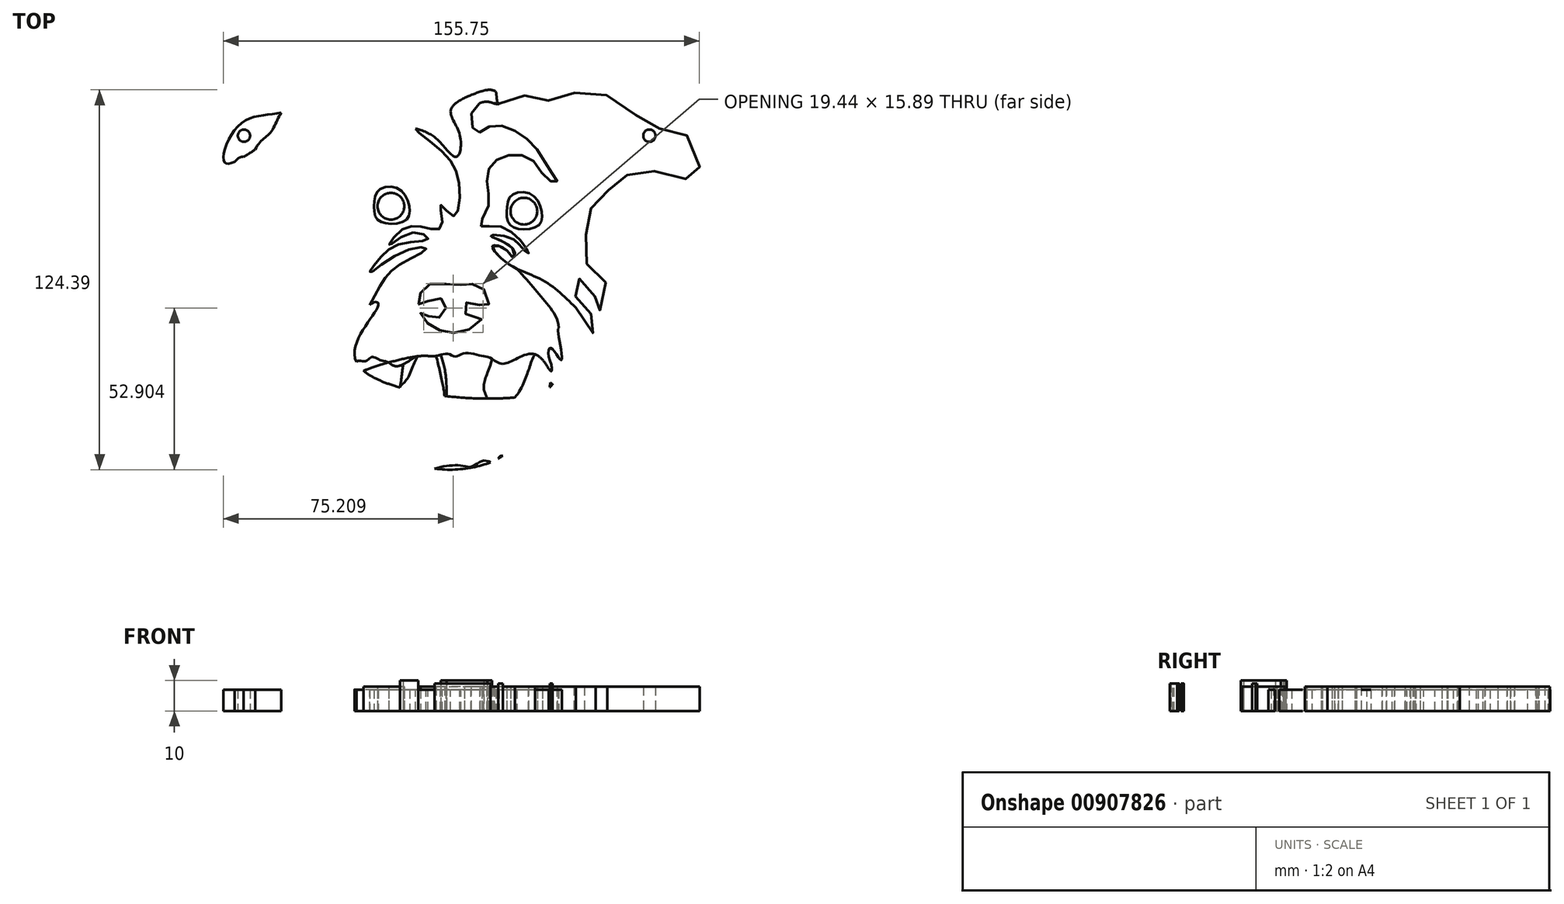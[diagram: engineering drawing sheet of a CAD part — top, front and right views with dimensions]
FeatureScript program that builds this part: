
annotation { "Feature Type Name" : "Feature", "Feature Type Description" : "" }
export const myFeature = defineFeature(function(context is Context, id is Id, definition is map)
    precondition{}
    {
        {
            var Q0;
            Q0=qCreatedBy(makeId("Top.planeOp"),FACE);
            var sketch = newSketch(context, id + "F0", { "sketchPlane" : qUnion([Q0])});
            skFitSpline(sketch, "E0", {"points": [v(-10.8, -4.8) * mm, v(-6.27, 3.26) * mm, v(0, 8.97) * mm, v(7.61, 13.52) * mm, v(0, 12.57) * mm, v(-10.8, 5.73) * mm, v(-8.15, 9.81) * mm, v(0, 15.35) * mm, v(8.27, 16.8) * mm, v(2.9, 18.78) * mm, v(-4.45, 14.71) * mm, v(0, 19.94) * mm, v(7.46, 20.4) * mm, v(12.68, 20.87) * mm, v(12.37, 27.92) * mm, v(16.54, 24.23) * mm, v(18.41, 34.41) * mm, v(12.68, 45.55) * mm, v(4.16, 52.76) * mm, v(7.78, 51.65) * mm, v(12.74, 47.87) * mm, v(17.51, 43.68) * mm, v(18.68, 50.57) * mm, v(15.7, 58.97) * mm, v(23.33, 64.27) * mm, v(30.48, 64.9) * mm, v(31.5, 61.05) * mm, v(27.68, 61.69) * mm, v(22.54, 58.18) * mm, v(24.15, 51.63) * mm, v(28.4, 53.58) * mm, v(36.06, 52.49) * mm, v(43.55, 46.57) * mm, v(48.61, 38.67) * mm, v(50.45, 35.49) * mm, v(47.6, 36.07) * mm, v(42.15, 42.8) * mm, v(34.73, 44.14) * mm, v(28.78, 40.89) * mm, v(27.59, 34.03) * mm, v(27.86, 27.2) * mm, v(25.33, 21.09) * mm, v(31.5, 20.96) * mm, v(39.88, 14.46) * mm, v(41.11, 12.07) * mm, v(38.85, 13.96) * mm, v(35.11, 17.25) * mm, v(28.71, 17.86) * mm, v(36.07, 13.55) * mm, v(36.16, 10.73) * mm, v(33.75, 13.27) * mm, v(29.39, 14.45) * mm, v(31.5, 11.05) * mm, v(37.36, 6.94) * mm, v(44.52, 3.89) * mm, v(50.99, -0.43) * mm, v(56.57, -5.75) * mm], "startDerivative": vector(204.5, 377.81) * mm, "endDerivative": vector(287.63, -276.69) * mm});
            skFitSpline(sketch, "E1", {"points": [v(8.8, 1.95) * mm, v(5.37, -1.97) * mm, v(5.52, -4.91) * mm, v(10.58, -2.48) * mm, v(14, -4.45) * mm, v(12.53, -8.54) * mm, v(9.6, -9.02) * mm, v(5.84, -7.37) * mm, v(7.8, -10.65) * mm, v(13.5, -13.46) * mm, v(20.67, -13.32) * mm, v(25.9, -9.08) * mm, v(23.61, -8.9) * mm, v(20.36, -7.42) * mm, v(21.5, -3.66) * mm, v(27.53, -5.65) * mm, v(26.73, 0) * mm, v(21.85, 2.07) * mm, v(17.44, 1.76) * mm, v(8.8, 1.95) * mm]});
            skFitSpline(sketch, "E2", {"points": [v(1.18, 23.1) * mm, v(2.05, 27.69) * mm, v(-1.63, 33.35) * mm, v(-7.8, 32.82) * mm, v(-9.32, 28.56) * mm, v(-8.65, 23.6) * mm, v(-4.68, 21.8) * mm, v(1.18, 23.1) * mm]});
            skFitSpline(sketch, "E3", {"points": [v(44.57, 21.3) * mm, v(45.44, 25.89) * mm, v(41.75, 31.54) * mm, v(35.58, 31.01) * mm, v(34.06, 26.75) * mm, v(34.73, 21.8) * mm, v(38.7, 19.99) * mm, v(44.57, 21.3) * mm]});
            skFitSpline(sketch, "E4", {"points": [v(-39.8, 58.13) * mm, v(-43.2, 51.74) * mm, v(-47.26, 47.79) * mm, v(-50.4, 42.92) * mm, v(-52.33, 43.63) * mm, v(-56.15, 40.35) * mm], "startDerivative": vector(-14.9, -24.98) * mm, "endDerivative": vector(-17.36, -29.51) * mm});
            skCircle(sketch, "E5", {"center": v(-3.88, 27.48) * mm, "radius": 4.38 * mm});
            skCircle(sketch, "E6", {"center": v(39.61, 25.85) * mm, "radius": 4.38 * mm});
            skFitSpline(sketch, "E7.trimOffspring", {"points": [v(-53.58, 42.72) * mm, v(-38.46, 50.37) * mm, v(-36.8, 41.61) * mm, v(-29.18, 37.15) * mm, v(-26.98, 27.78) * mm, v(-25.92, 22.85) * mm, v(-32.23, 11.83) * mm, v(-35, 4.15) * mm, v(-39.11, -7.41) * mm, v(-35.05, -17) * mm, v(-33.9, -6.88) * mm, v(-30.1, -3.66) * mm, v(-29.82, -7.15) * mm, v(-31.18, -15.42) * mm, v(-26.03, -25.03) * mm, v(-28.42, -13.22) * mm, v(-25.45, -8.9) * mm, v(-24.9, -17.09) * mm, v(-21.64, -29.95) * mm, v(-21.75, -14.74) * mm, v(-18.15, -10.31) * mm, v(-16.36, -15.67) * mm, v(-10.8, -4.8) * mm, v(-7.98, -4.63) * mm, v(-15.2, -23.55) * mm, v(47.9, -31.99) * mm, v(47.73, -21.57) * mm, v(48.51, -18.94) * mm, v(51.72, -22.93) * mm, v(51.36, -17.05) * mm, v(51.05, -12.37) * mm, v(54.1, -14.13) * mm, v(59.32, -20.41) * mm, v(57.39, -12) * mm, v(56.56, -5.73) * mm, v(62.83, -14.58) * mm, v(59.75, -4.42) * mm, v(56.29, -1.7) * mm, v(57.41, 3.6) * mm, v(62.47, -0.53) * mm, v(63.7, -7.26) * mm, v(66.76, 1.24) * mm, v(60.44, 8.2) * mm, v(60.2, 19.77) * mm, v(62.4, 28.3) * mm, v(69.28, 34.33) * mm, v(75.06, 38.45) * mm, v(88.21, 37.84) * mm, v(96.19, 36.7) * mm, v(94.02, 49.67) * mm, v(83.59, 53) * mm, v(74.28, 58.82) * mm, v(59.76, 65.5) * mm, v(48.51, 61.93) * mm, v(41.1, 63.9) * mm, v(31.5, 61.05) * mm, v(30.5, 64.89) * mm, v(27.96, 67.2) * mm, v(17.53, 66.47) * mm, v(12.86, 62.32) * mm, v(4.92, 67.63) * mm, v(2.17, 64.3) * mm, v(-4.68, 62.96) * mm, v(-8.27, 61.58) * mm, v(-18.94, 67.15) * mm, v(-29.1, 63.32) * mm, v(-39.8, 58.13) * mm, v(-53.18, 54.38) * mm, v(-58.52, 42.2) * mm, v(-53.58, 42.72) * mm]});
            skCircle(sketch, "E8", {"center": v(-51.96, 50.57) * mm, "radius": 2 * mm});
            skLineSegment(sketch, "E9", {"start": v(-51.96, 50.57) * mm, "end": v(80.66, 50.57) * mm, "construction": true});
            skCircle(sketch, "E10", {"center": v(80.66, 50.57) * mm, "radius": 2 * mm});
            skPoint(sketch, "E11.startDerivative.orphan", {"position": v(46.68, -34.89) * mm});
            skPoint(sketch, "E12.23.internal.orphan", {"position": v(-8.15, -6.56) * mm});
            skPoint(sketch, "E12.45.internal.orphan", {"position": v(66.75, 0) * mm});
            skPoint(sketch, "E12.5.internal.orphan", {"position": v(-25.9, 21.6) * mm});
            skFitSpline(sketch, "E13", {"points": [v(48.07, -31.84) * mm, v(47.73, -25.71) * mm, v(43.27, -21.01) * mm, v(36.6, -22.74) * mm, v(31.89, -24.02) * mm, v(28.43, -22.1) * mm, v(25.22, -21.45) * mm, v(20.4, -20.58) * mm, v(17.3, -21.71) * mm, v(14.66, -20.83) * mm, v(10.88, -21.54) * mm, v(5.07, -21.63) * mm, v(-13.12, -26.56) * mm], "startDerivative": vector(16.73, 149.66) * mm, "endDerivative": vector(-59.85, -28.24) * mm});
            skFitSpline(sketch, "E14", {"points": [v(-11.13, -25.98) * mm, v(-2.47, -37.25) * mm, v(-2.3, -42.9) * mm, v(-0.8, -48.97) * mm, v(2.37, -53.28) * mm, v(7.48, -55.7) * mm, v(10.82, -55.22) * mm, v(16.1, -55.92) * mm, v(18.48, -55.4) * mm, v(21.3, -54.25) * mm, v(24.73, -50.64) * mm, v(27.54, -46.24) * mm, v(27.28, -42.02) * mm, v(28.34, -37.97) * mm, v(26.49, -31.8) * mm, v(29.15, -22.5) * mm], "startDerivative": vector(45.21, -72.34) * mm, "endDerivative": vector(22.44, 125.56) * mm});
            skFitSpline(sketch, "E15", {"points": [v(-2.47, -37.25) * mm, v(-0.97, -31.84) * mm, v(0.45, -23.07) * mm], "startDerivative": vector(-0.31, 9) * mm, "endDerivative": vector(3.22, 7.67) * mm});
            skFitSpline(sketch, "E16", {"points": [v(10.88, -21.54) * mm, v(13.16, -31.45) * mm, v(13.6, -37.25) * mm, v(12.04, -48.13) * mm, v(12.29, -50) * mm, v(13.42, -45.91) * mm, v(14.28, -31.84) * mm, v(13.48, -24.82) * mm, v(12.42, -21.16) * mm], "startDerivative": vector(18.26, -65.77) * mm, "endDerivative": vector(-11.6, 37.87) * mm});
            skFitSpline(sketch, "E17", {"points": [v(-21.75, -14.74) * mm, v(-18.15, -32.84) * mm, v(-10.83, -43.87) * mm, v(-8.52, -51.1) * mm, v(-6.1, -54.56) * mm, v(-4.05, -53.13) * mm, v(-1.19, -58.8) * mm, v(2.45, -56.73) * mm, v(6.48, -58.59) * mm, v(12.34, -57.95) * mm, v(19.06, -57.47) * mm, v(22.65, -57.77) * mm, v(26.74, -55.8) * mm, v(30.13, -56.63) * mm, v(31.89, -54.36) * mm, v(34.45, -54.33) * mm, v(39.8, -47.91) * mm, v(45.11, -40.35) * mm, v(47.73, -25.71) * mm], "startDerivative": vector(14.83, -144.66) * mm, "endDerivative": vector(20.53, 124.04) * mm});
            skFitSpline(sketch, "E18", {"points": [v(-21.64, -29.95) * mm, v(-21.77, -32.8) * mm, v(-21.65, -40.38) * mm, v(-8.75, -50.33) * mm, v(9.3, -58.25) * mm, v(28.4, -56.49) * mm, v(39.8, -47.91) * mm, v(48.07, -31.84) * mm], "startDerivative": vector(-2.7, -16.77) * mm, "endDerivative": vector(-32.2, 87.54) * mm});
            skFitSpline(sketch, "E19", {"points": [v(-21.7, -31.76) * mm, v(-20.96, -30.57) * mm, v(-19.47, -29.17) * mm], "startDerivative": vector(1.6, 2.32) * mm, "endDerivative": vector(0.83, 1.94) * mm});
            skFitSpline(sketch, "E20", {"points": [v(7.48, -55.7) * mm, v(0.94, -54.98) * mm, v(-3.23, -52.53) * mm, v(-4.81, -46.85) * mm, v(-6.3, -43.16) * mm, v(-8.77, -37.79) * mm, v(-10.27, -31.89) * mm, v(-12.43, -26.75) * mm], "startDerivative": vector(-37.93, 0.45) * mm, "endDerivative": vector(-25.79, 34.44) * mm});
            skFitSpline(sketch, "E21", {"points": [v(5.07, -21.63) * mm, v(1.63, -28.75) * mm, v(-0.97, -31.84) * mm], "startDerivative": vector(-5.85, -5.23) * mm, "endDerivative": vector(-4.71, -8.1) * mm});
            skFitSpline(sketch, "E22", {"points": [v(5.07, -21.63) * mm, v(1.09, -23.8) * mm, v(-2.67, -24.86) * mm, v(-4.94, -23.53) * mm, v(-7.66, -22.8) * mm, v(-10.22, -21.88) * mm, v(-12.36, -23.26) * mm, v(-15.2, -23.55) * mm], "startDerivative": vector(-20.84, -2.18) * mm, "endDerivative": vector(-14.68, -20.72) * mm});
            skFitSpline(sketch, "E23", {"points": [v(48.57, -24.37) * mm, v(48.6, -26.55) * mm, v(47.73, -25.71) * mm], "startDerivative": vector(0.43, -1.1) * mm, "endDerivative": vector(-0.72, 0.67) * mm});
            skLineSegment(sketch, "E24.trimOffspring", {"start": v(51.23, -22.45) * mm, "end": v(51.23, -22.45) * mm});
            skFitSpline(sketch, "E25.trimOffspring", {"points": [v(30.15, 61.06) * mm, v(29.84, 61.06) * mm, v(31.5, 61.05) * mm], "startDerivative": vector(2.35, 0.22) * mm, "endDerivative": vector(2.29, -1.15) * mm});
            skFitSpline(sketch, "E26.trimOffspring", {"points": [v(-10.8, -4.8) * mm, v(-6.27, 3.26) * mm, v(0, 8.97) * mm, v(7.61, 13.52) * mm, v(0, 12.57) * mm, v(-10.8, 5.73) * mm, v(-8.15, 9.81) * mm, v(0, 15.35) * mm, v(8.27, 16.8) * mm, v(2.9, 18.78) * mm, v(-4.45, 14.71) * mm, v(0, 19.94) * mm, v(7.46, 20.4) * mm, v(12.68, 20.87) * mm, v(12.37, 27.92) * mm, v(16.54, 24.23) * mm, v(18.41, 34.41) * mm, v(12.68, 45.55) * mm, v(4.16, 52.76) * mm, v(7.78, 51.65) * mm, v(12.74, 47.87) * mm, v(17.51, 43.68) * mm, v(18.68, 50.62) * mm, v(15.7, 58.97) * mm, v(23.33, 64.27) * mm, v(30.48, 64.9) * mm, v(31.5, 61.05) * mm, v(27.68, 61.69) * mm, v(22.54, 58.18) * mm, v(24.15, 51.63) * mm, v(28.4, 53.58) * mm, v(36.06, 52.49) * mm, v(43.55, 46.57) * mm, v(48.61, 38.67) * mm, v(50.45, 35.49) * mm, v(47.6, 36.07) * mm, v(42.15, 42.8) * mm, v(34.73, 44.14) * mm, v(28.78, 40.89) * mm, v(27.59, 34.03) * mm, v(27.86, 27.2) * mm, v(25.33, 21.09) * mm, v(31.5, 20.96) * mm, v(39.88, 14.46) * mm, v(41.11, 12.07) * mm, v(38.85, 13.96) * mm, v(35.11, 17.25) * mm, v(28.71, 17.86) * mm, v(36.07, 13.55) * mm, v(36.16, 10.73) * mm, v(33.75, 13.27) * mm, v(29.39, 14.45) * mm, v(31.5, 11.05) * mm, v(37.36, 6.94) * mm, v(44.52, 3.89) * mm, v(50.99, -0.43) * mm, v(56.57, -5.75) * mm], "startDerivative": vector(204.5, 377.81) * mm, "endDerivative": vector(287.63, -276.69) * mm});
            skLineSegment(sketch, "E27", {"start": v(-8.75, -50.33) * mm, "end": v(38.15, -50.33) * mm, "construction": true});
            skFitSpline(sketch, "E28", {"points": [v(38.15, -50.33) * mm, v(48.61, -43.38) * mm, v(50.14, -40.66) * mm, v(50.77, -38.4) * mm, v(50.88, -34.2) * mm, v(50.82, -32.87) * mm, v(49.65, -31.36) * mm, v(47.21, -29.67) * mm], "startDerivative": vector(50.7, 11.43) * mm, "endDerivative": vector(-15.7, 6.64) * mm});
            skFitSpline(sketch, "E29", {"points": [v(0.94, -54.98) * mm, v(7.36, -56.11) * mm, v(10.41, -55.7) * mm], "startDerivative": vector(11.84, -2.87) * mm, "endDerivative": vector(6.81, 1.99) * mm});
            skFitSpline(sketch, "E30.trimOffspring", {"points": [v(7.48, -55.57) * mm, v(10.4, -55.69) * mm, v(12.88, -56.53) * mm, v(18.22, -56.58) * mm, v(25.86, -54.07) * mm, v(28.17, -51.56) * mm, v(30, -45.33) * mm, v(32.67, -39.36) * mm, v(37.27, -34.44) * mm, v(40.1, -29) * mm, v(41.56, -24.92) * mm, v(43.27, -21.01) * mm], "startDerivative": vector(44.21, 4.46) * mm, "endDerivative": vector(27.63, 35.75) * mm});
            skFitSpline(sketch, "E31", {"points": [v(37.36, 6.94) * mm, v(43.45, 0) * mm, v(48.1, -5.63) * mm, v(51.05, -12.37) * mm], "startDerivative": vector(19.78, -20.54) * mm, "endDerivative": vector(1.27, -26.57) * mm});
            skFitSpline(sketch, "E32.trimOffspring", {"points": [v(-10.8, -4.8) * mm, v(-6.27, 3.26) * mm, v(0, 8.97) * mm, v(7.61, 13.52) * mm, v(0, 12.57) * mm, v(-10.8, 5.73) * mm, v(-8.15, 9.81) * mm, v(0, 15.35) * mm, v(8.27, 16.8) * mm, v(2.9, 18.78) * mm, v(-4.45, 14.71) * mm, v(0, 19.94) * mm, v(7.46, 20.4) * mm, v(12.68, 20.87) * mm, v(12.37, 27.92) * mm, v(16.54, 24.23) * mm, v(18.41, 34.41) * mm, v(12.68, 45.55) * mm, v(4.16, 52.76) * mm, v(7.78, 51.65) * mm, v(12.74, 47.87) * mm, v(17.51, 43.68) * mm, v(18.68, 50.62) * mm, v(15.7, 58.97) * mm, v(23.33, 64.27) * mm, v(30.48, 64.9) * mm, v(31.5, 61.05) * mm, v(27.68, 61.69) * mm, v(22.54, 58.18) * mm, v(24.15, 51.63) * mm, v(28.4, 53.58) * mm, v(36.06, 52.49) * mm, v(43.55, 46.57) * mm, v(48.61, 38.67) * mm, v(50.45, 35.49) * mm, v(47.6, 36.07) * mm, v(42.15, 42.8) * mm, v(34.73, 44.14) * mm, v(28.78, 40.89) * mm, v(27.59, 34.03) * mm, v(27.86, 27.2) * mm, v(25.33, 21.09) * mm, v(31.5, 20.96) * mm, v(39.88, 14.46) * mm, v(41.11, 12.07) * mm, v(38.85, 13.96) * mm, v(35.11, 17.25) * mm, v(28.71, 17.86) * mm, v(36.07, 13.55) * mm, v(36.16, 10.73) * mm, v(33.75, 13.27) * mm, v(29.39, 14.45) * mm, v(31.5, 11.05) * mm, v(37.36, 6.94) * mm, v(44.52, 3.89) * mm, v(50.99, -0.43) * mm, v(56.57, -5.75) * mm], "startDerivative": vector(204.5, 377.81) * mm, "endDerivative": vector(287.63, -276.69) * mm});
            skSolve(sketch);
        }
        {
            var Q0;
            {var subQ1=sQuery(id+"F0.wireOp",EDGE,"E0");Q0=makeQuery(id+"F0.imprint","IMPRINT",FACE,{"disambiguationData":[TD([[makeQuery(id+"F0.imprint","IMPRINT",EDGE,{"derivedFrom":subQ1}),-1.0]])]});}
            var Q1;
            Q1=makeQuery(id+"F0.imprint","IMPRINT",FACE,{"disambiguationData":[TD([[makeQuery(id+"F0.imprint","IMPRINT",EDGE,{"derivedFrom":sQuery(id+"F0.wireOp",EDGE,"E3")}),1.0]])]});
            var Q2;
            Q2=makeQuery(id+"F0.imprint","IMPRINT",FACE,{"disambiguationData":[TD([[makeQuery(id+"F0.imprint","IMPRINT",EDGE,{"derivedFrom":sQuery(id+"F0.wireOp",EDGE,"E2")}),1.0]])]});
            var Q3;
            Q3=makeQuery(id+"F0.imprint","IMPRINT",FACE,{"disambiguationData":[TD([[makeQuery(id+"F0.imprint","IMPRINT",EDGE,{"derivedFrom":sQuery(id+"F0.wireOp",EDGE,"E8")}),-1.0]])]});
            var Q4;
            {var subQ0=sQuery(id+"F0.wireOp",EDGE,"E7.trimOffspring");var subQ1=sQuery(id+"F0.wireOp",EDGE,"E4");var subQ2=makeQuery(id+"F0.imprint","INTERSECT",VERTEX,{"disambiguationData":[OD(1.0)],"derivedFrom":[subQ1,subQ0]});Q4=makeQuery(id+"F0.imprint","IMPRINT",FACE,{"disambiguationData":[TD([[makeQuery(id+"F0.imprint","IMPRINT",EDGE,{"disambiguationData":[TD([[subQ2,-1.0]])],"derivedFrom":subQ1}),1.0]])]});}
            var Q5;
            {var subQ3=sQuery(id+"F0.wireOp",EDGE,"E7.trimOffspring");var subQ11=makeQuery(id+"F0.imprint","INTERSECT",VERTEX,{"disambiguationData":[OD(0.0)],"derivedFrom":[sQuery(id+"F0.wireOp",EDGE,"E0"),subQ3]});Q5=makeQuery(id+"F0.imprint","IMPRINT",FACE,{"disambiguationData":[TD([[makeQuery(id+"F0.imprint","IMPRINT",EDGE,{"disambiguationData":[TD([[subQ11,1.0]])],"derivedFrom":subQ3}),-1.0]])]});}
            extrude(context, id + "F1", {"entities" : qUnion([Q0, Q1, Q2, Q3, Q4, Q5]), "depth" : 7 * mm, "offsetDistance" : 25 * mm});
        }
        {
            var Q0;
            {var subQ0=sQuery(id+"F0.wireOp",EDGE,"E16");Q0=makeQuery(id+"F0.imprint","IMPRINT",FACE,{"disambiguationData":[TD([[makeQuery(id+"F0.imprint","IMPRINT",EDGE,{"derivedFrom":subQ0}),1.0]])]});}
            var Q1;
            {var subQ3=sQuery(id+"F0.wireOp",EDGE,"E15");Q1=makeQuery(id+"F0.imprint","IMPRINT",FACE,{"disambiguationData":[TD([[makeQuery(id+"F0.imprint","IMPRINT",EDGE,{"derivedFrom":subQ3}),1.0]])]});}
            var Q2;
            {var subQ0=sQuery(id+"F0.wireOp",EDGE,"E14");var subQ1=sQuery(id+"F0.wireOp",EDGE,"E13");var subQ2=makeQuery(id+"F0.imprint","INTERSECT",VERTEX,{"disambiguationData":[OD(1.0)],"derivedFrom":[subQ1,subQ0]});Q2=makeQuery(id+"F0.imprint","IMPRINT",FACE,{"disambiguationData":[TD([[makeQuery(id+"F0.imprint","IMPRINT",EDGE,{"disambiguationData":[TD([[subQ2,1.0]])],"derivedFrom":subQ1}),1.0]])]});}
            var Q3;
            Q3=makeQuery(id+"F0.imprint","IMPRINT",FACE,{"disambiguationData":[TD([[makeQuery(id+"F0.imprint","IMPRINT",EDGE,{"derivedFrom":sQuery(id+"F0.wireOp",EDGE,"E1")}),1.0]])]});
            var Q4;
            {var subQ4=sQuery(id+"F0.wireOp",EDGE,"E0");Q4=makeQuery(id+"F0.imprint","IMPRINT",FACE,{"disambiguationData":[TD([[makeQuery(id+"F0.imprint","IMPRINT",EDGE,{"derivedFrom":subQ4}),1.0]])]});}
            var Q5;
            Q5=makeQuery(id+"F0.imprint","IMPRINT",FACE,{"disambiguationData":[TD([[makeQuery(id+"F0.imprint","IMPRINT",EDGE,{"derivedFrom":sQuery(id+"F0.wireOp",EDGE,"E5")}),1.0]])]});
            var Q6;
            Q6=makeQuery(id+"F0.imprint","IMPRINT",FACE,{"disambiguationData":[TD([[makeQuery(id+"F0.imprint","IMPRINT",EDGE,{"derivedFrom":sQuery(id+"F0.wireOp",EDGE,"E6")}),1.0]])]});
            var Q7;
            Q7=makeQuery(id+"F0.imprint","IMPRINT",FACE,{"disambiguationData":[TD([[makeQuery(id+"F0.imprint","IMPRINT",EDGE,{"derivedFrom":sQuery(id+"F0.wireOp",EDGE,"E3")}),-1.0]])]});
            extrude(context, id + "F2", {"entities" : qUnion([Q0, Q1, Q2, Q3, Q4, Q5, Q6, Q7]), "depth" : 8 * mm, "offsetDistance" : 25 * mm});
        }
        {
            var Q0;
            {var subQ0=sQuery(id+"F0.wireOp",EDGE,"0c20575f-e394-47d6-a4be-a032e933ec21");Q0=makeQuery(id+"F0.imprint","IMPRINT",FACE,{"disambiguationData":[TD([[makeQuery(id+"F0.imprint","IMPRINT",EDGE,{"derivedFrom":subQ0}),1.0]])]});}
            var Q1;
            {var subQ0=sQuery(id+"F0.wireOp",EDGE,"E18");Q1=makeQuery(id+"F0.imprint","IMPRINT",FACE,{"disambiguationData":[TD([[makeQuery(id+"F0.imprint","IMPRINT",EDGE,{"derivedFrom":subQ0}),1.0]])]});}
            var Q2;
            {var subQ2=sQuery(id+"F0.wireOp",EDGE,"a8659436-59ba-4290-a117-f28557bdea4d");Q2=makeQuery(id+"F0.imprint","IMPRINT",FACE,{"disambiguationData":[TD([[makeQuery(id+"F0.imprint","IMPRINT",EDGE,{"derivedFrom":subQ2}),1.0]])]});}
            var Q3;
            {var subQ0=sQuery(id+"F0.wireOp",EDGE,"E28");Q3=makeQuery(id+"F0.imprint","IMPRINT",FACE,{"disambiguationData":[TD([[makeQuery(id+"F0.imprint","IMPRINT",EDGE,{"derivedFrom":subQ0}),1.0]])]});}
            extrude(context, id + "F3", {"entities" : qUnion([Q0, Q1, Q2, Q3]), "operationType" : NewBodyOperationType.ADD, "depth" : 9 * mm, "offsetDistance" : 25 * mm});
        }
        {
            var Q0;
            {var subQ6=sQuery(id+"F0.wireOp",EDGE,"E15");Q0=makeQuery(id+"F0.imprint","IMPRINT",FACE,{"disambiguationData":[TD([[makeQuery(id+"F0.imprint","IMPRINT",EDGE,{"derivedFrom":subQ6}),-1.0]])]});}
            var Q1;
            {var subQ4=sQuery(id+"F0.wireOp",EDGE,"E16");Q1=makeQuery(id+"F0.imprint","IMPRINT",FACE,{"disambiguationData":[TD([[makeQuery(id+"F0.imprint","IMPRINT",EDGE,{"derivedFrom":subQ4}),-1.0]])]});}
            extrude(context, id + "F4", {"entities" : qUnion([Q0, Q1]), "depth" : 10 * mm, "offsetDistance" : 25 * mm});
        }
    });
